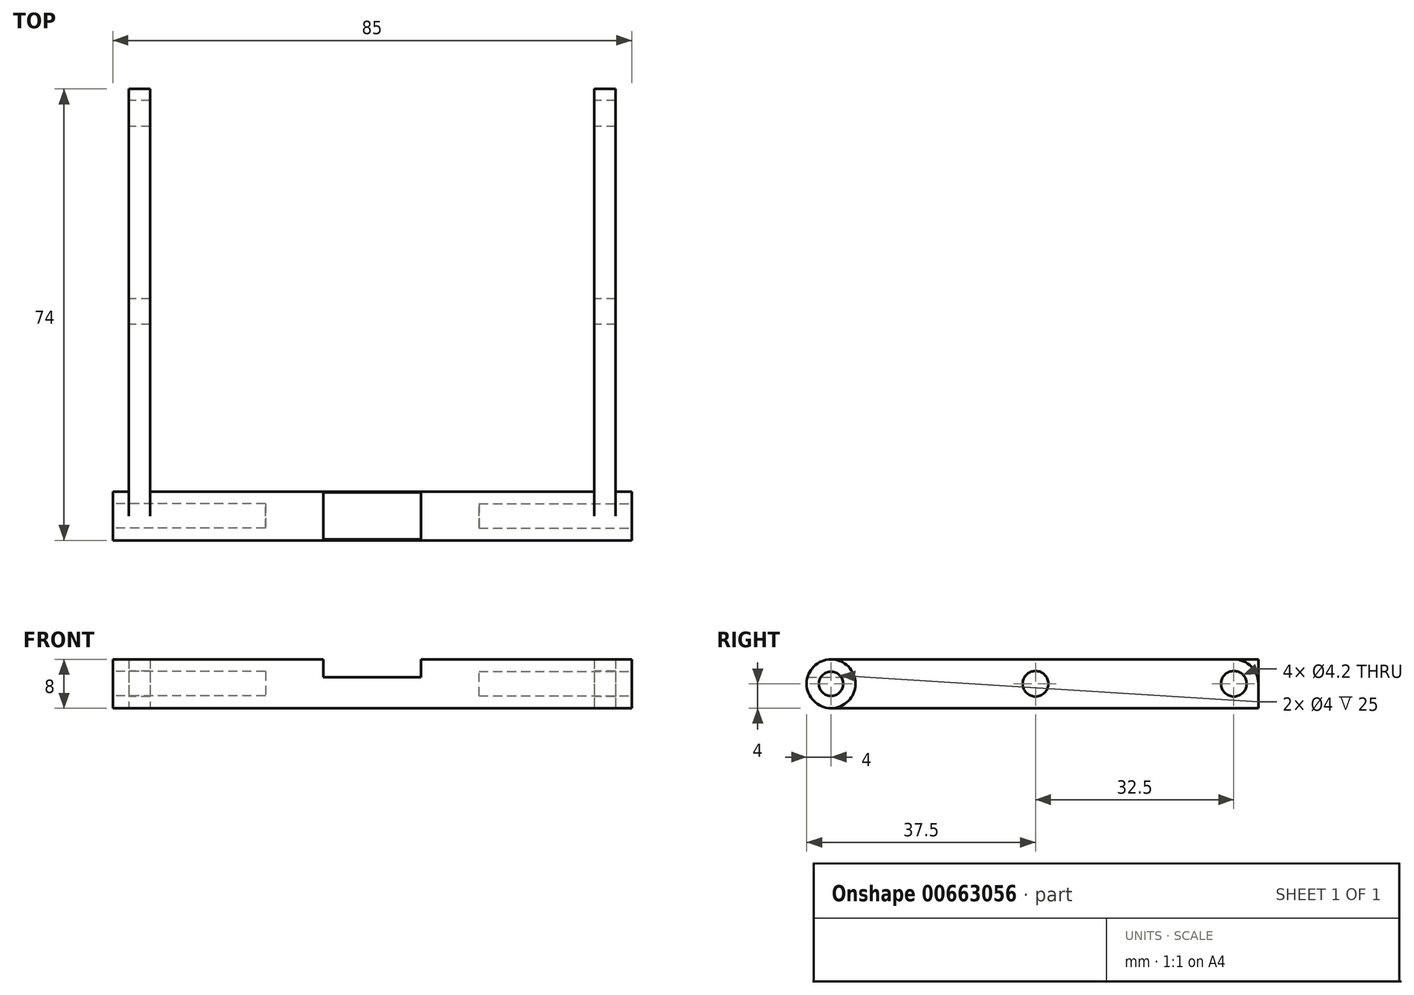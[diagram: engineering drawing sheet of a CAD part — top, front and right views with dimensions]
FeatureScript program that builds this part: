
annotation { "Feature Type Name" : "Feature", "Feature Type Description" : "" }
export const myFeature = defineFeature(function(context is Context, id is Id, definition is map)
    precondition{}
    {
        {
            var Q0;
            Q0=qCreatedBy(makeId("Right.planeOp"),FACE);
            var sketch = newSketch(context, id + "F0", { "sketchPlane" : qUnion([Q0])});
            skCircle(sketch, "E0", {"center": v(0, 0) * mm, "radius": 4 * mm});
            skSolve(sketch);
        }
        {
            var Q0;
            Q0 = qSketchRegion(id + "F0", true);
            extrude(context, id + "F1", {"entities" : qUnion([Q0]), "depth" : 42.5 * mm, "offsetDistance" : 25 * mm, "hasSecondDirection" : true, "secondDirectionOppositeDirection" : true, "secondDirectionDepth" : 42.5 * mm});
        }
        {
            var Q0;
            Q0=qCreatedBy(makeId("Top.planeOp"),FACE);
            var sketch = newSketch(context, id + "F2", { "sketchPlane" : qUnion([Q0])});
            skLineSegment(sketch, "E1", {"start": v(-42.5, 4) * mm, "end": v(42.5, 4) * mm});
            skLineSegment(sketch, "E2", {"start": v(42.5, -4) * mm, "end": v(-42.5, -4) * mm});
            skLineSegment(sketch, "E3.bottom", {"start": v(0, 4) * mm, "end": v(8, 4) * mm});
            skLineSegment(sketch, "E3.top", {"start": v(0, -4) * mm, "end": v(8, -4) * mm});
            skLineSegment(sketch, "E3.left", {"start": v(0, 4) * mm, "end": v(0, -4) * mm});
            skLineSegment(sketch, "E3.right", {"start": v(8, 4) * mm, "end": v(8, -4) * mm});
            skLineSegment(sketch, "E4.MirrorCS", {"start": v(42.5, 4) * mm, "end": v(-42.5, 4) * mm});
            skLineSegment(sketch, "E5.MirrorCS", {"start": v(-8, 4) * mm, "end": v(-8, -4) * mm});
            skSolve(sketch);
        }
        {
            var Q0;
            Q0 = qSketchRegion(id + "F2", true);
            extrude(context, id + "F3", {"entities" : qUnion([Q0]), "operationType" : NewBodyOperationType.REMOVE, "depth" : 25 * mm, "offsetDistance" : 25 * mm});
        }
        {
            var Q0;
            Q0=qCreatedBy(makeId("Front.planeOp"),FACE);
            var sketch = newSketch(context, id + "F4", { "sketchPlane" : qUnion([Q0])});
            skLineSegment(sketch, "E6", {"start": v(-42.5, 4) * mm, "end": v(-42.38, 4) * mm});
            skLineSegment(sketch, "E7", {"start": v(39.88, -4) * mm, "end": v(36.38, -4) * mm});
            skLineSegment(sketch, "E8.bottom", {"start": v(39.88, 4) * mm, "end": v(36.38, 4) * mm});
            skLineSegment(sketch, "E8.left", {"start": v(39.88, 4) * mm, "end": v(39.88, -4) * mm});
            skLineSegment(sketch, "E8.right", {"start": v(36.38, 4) * mm, "end": v(36.38, -4) * mm});
            skLineSegment(sketch, "E9", {"start": v(0, 23.06) * mm, "end": v(0, -23.5) * mm, "construction": true});
            skLineSegment(sketch, "E10.MirrorCS", {"start": v(-39.88, -4) * mm, "end": v(-36.38, -4) * mm});
            skLineSegment(sketch, "E11.MirrorCS", {"start": v(-39.88, 4) * mm, "end": v(-36.38, 4) * mm});
            skLineSegment(sketch, "E12.MirrorCS", {"start": v(-36.38, 4) * mm, "end": v(-36.38, -4) * mm});
            skLineSegment(sketch, "E13.MirrorCS", {"start": v(-39.88, 4) * mm, "end": v(-39.88, -4) * mm});
            skLineSegment(sketch, "E14.MirrorCS", {"start": v(42.5, 4) * mm, "end": v(42.38, 4) * mm});
            skLineSegment(sketch, "E15.trimOffspring", {"start": v(36.38, 4) * mm, "end": v(39.88, 4) * mm});
            skLineSegment(sketch, "E16.trimOffspring", {"start": v(-36.38, -4) * mm, "end": v(-39.88, -4) * mm});
            skPoint(sketch, "E17.orphan", {"position": v(42.38, 4) * mm});
            skPoint(sketch, "E18.orphan", {"position": v(42.5, -4) * mm});
            skPoint(sketch, "E19.orphan", {"position": v(-42.5, -4) * mm});
            skLineSegment(sketch, "E20.trimOffspring", {"start": v(36.38, -4) * mm, "end": v(39.88, -4) * mm});
            skLineSegment(sketch, "E21.trimOffspring", {"start": v(-36.38, 4) * mm, "end": v(-39.88, 4) * mm});
            skSolve(sketch);
        }
        {
            var Q0;
            Q0 = qSketchRegion(id + "F4", true);
            extrude(context, id + "F5", {"entities" : qUnion([Q0]), "operationType" : NewBodyOperationType.ADD, "oppositeDirection" : true, "depth" : 70 * mm, "offsetDistance" : 25 * mm});
        }
        {
            var Q0;
            Q0=makeQuery(id+"F1.opExtrude","CAP_FACE",FACE,{"disambiguationData":[OSD([sQuery(id+"F0.wireOp",EDGE,"E0")])],"isStart":false});
            var sketch = newSketch(context, id + "F6", { "sketchPlane" : qUnion([Q0])});
            skCircle(sketch, "E22", {"center": v(0, 0) * mm, "radius": 2 * mm});
            skSolve(sketch);
        }
        {
            var Q0;
            Q0 = qSketchRegion(id + "F6", true);
            extrude(context, id + "F7", {"entities" : qUnion([Q0]), "operationType" : NewBodyOperationType.REMOVE, "oppositeDirection" : true, "depth" : 25 * mm, "offsetDistance" : 25 * mm});
        }
        {
            var Q0;
            Q0=makeQuery(id+"F1.opExtrude","CAP_FACE",FACE,{"disambiguationData":[OSD([sQuery(id+"F0.wireOp",EDGE,"E0")])],"isStart":true});
            var sketch = newSketch(context, id + "F8", { "sketchPlane" : qUnion([Q0])});
            skCircle(sketch, "E23", {"center": v(0, 0) * mm, "radius": 2 * mm});
            skSolve(sketch);
        }
        {
            var Q0;
            Q0 = qSketchRegion(id + "F8", true);
            extrude(context, id + "F9", {"entities" : qUnion([Q0]), "operationType" : NewBodyOperationType.REMOVE, "oppositeDirection" : true, "depth" : 25 * mm, "offsetDistance" : 25 * mm});
        }
        {
            var Q0;
            Q0=makeQuery(id+"F5.opExtrude","CAP_EDGE",EDGE,{"disambiguationData":[OSD([sQuery(id+"F4.wireOp",EDGE,"E8.bottom")])],"isStart":false});
            var Q1;
            Q1=makeQuery(id+"F5.opExtrude","CAP_EDGE",EDGE,{"disambiguationData":[OSD([sQuery(id+"F4.wireOp",EDGE,"E20.trimOffspring")])],"isStart":false});
            var Q2;
            Q2=makeQuery(id+"F5.opExtrude","CAP_EDGE",EDGE,{"disambiguationData":[OSD([sQuery(id+"F4.wireOp",EDGE,"E21.trimOffspring")])],"isStart":false});
            var Q3;
            Q3=makeQuery(id+"F5.opExtrude","CAP_EDGE",EDGE,{"disambiguationData":[OSD([sQuery(id+"F4.wireOp",EDGE,"E16.trimOffspring")])],"isStart":false});
            fillet(context, id + "F10", {"entities" : qUnion([Q0, Q1, Q2, Q3]), "radius" : 4 * mm, "tangentPropagation" : true, "allowEdgeOverflow" : false});
        }
        {
            var Q0;
            Q0=makeQuery(id+"F5.opExtrude","SWEPT_FACE",FACE,{"disambiguationData":[OSD([sQuery(id+"F4.wireOp",EDGE,"E13.MirrorCS")])]});
            var sketch = newSketch(context, id + "F11", { "sketchPlane" : qUnion([Q0])});
            skCircle(sketch, "E24", {"center": v(-66, 0) * mm, "radius": 2.1 * mm});
            skCircle(sketch, "E25", {"center": v(-33.5, 0) * mm, "radius": 2.1 * mm});
            skSolve(sketch);
        }
        {
            var Q0;
            Q0 = qSketchRegion(id + "F11", true);
            extrude(context, id + "F12", {"entities" : qUnion([Q0]), "operationType" : NewBodyOperationType.REMOVE, "endBound" : BoundingType.THROUGH_ALL, "oppositeDirection" : true, "depth" : 25 * mm, "offsetDistance" : 25 * mm});
        }
        {
            var Q0;
            Q0=makeQuery(id+"F3.boolean.opBoolean","COPY",FACE,{"derivedFrom":makeQuery(id+"F3.opExtrude","SWEPT_FACE",FACE,{"disambiguationData":[OSD([sQuery(id+"F2.wireOp",EDGE,"E3.right")])]})});
            var sketch = newSketch(context, id + "F13", { "sketchPlane" : qUnion([Q0])});
            skLineSegment(sketch, "E26.0.0", {"start": v(-4, 0) * mm, "end": v(4, 0) * mm});
            skArc(sketch, "E26.0.1", {"start": v(4, 0) * mm, "mid": v(0, 4) * mm, "end": v(-4, 0) * mm});
            skLineSegment(sketch, "E27", {"start": v(-3.85, 1.1) * mm, "end": v(3.85, 1.1) * mm});
            skSolve(sketch);
        }
        {
            var Q0;
            {var subQ0=sQuery(id+"F13.wireOp",EDGE,"E26.0.0");Q0=makeQuery(id+"F13.imprint","IMPRINT",FACE,{"disambiguationData":[TD([[makeQuery(id+"F13.imprint","IMPRINT",EDGE,{"derivedFrom":subQ0}),1.0]])]});}
            extrude(context, id + "F14", {"entities" : qUnion([Q0]), "operationType" : NewBodyOperationType.ADD, "endBound" : BoundingType.UP_TO_NEXT, "depth" : 25 * mm, "offsetDistance" : 25 * mm});
        }
    });
